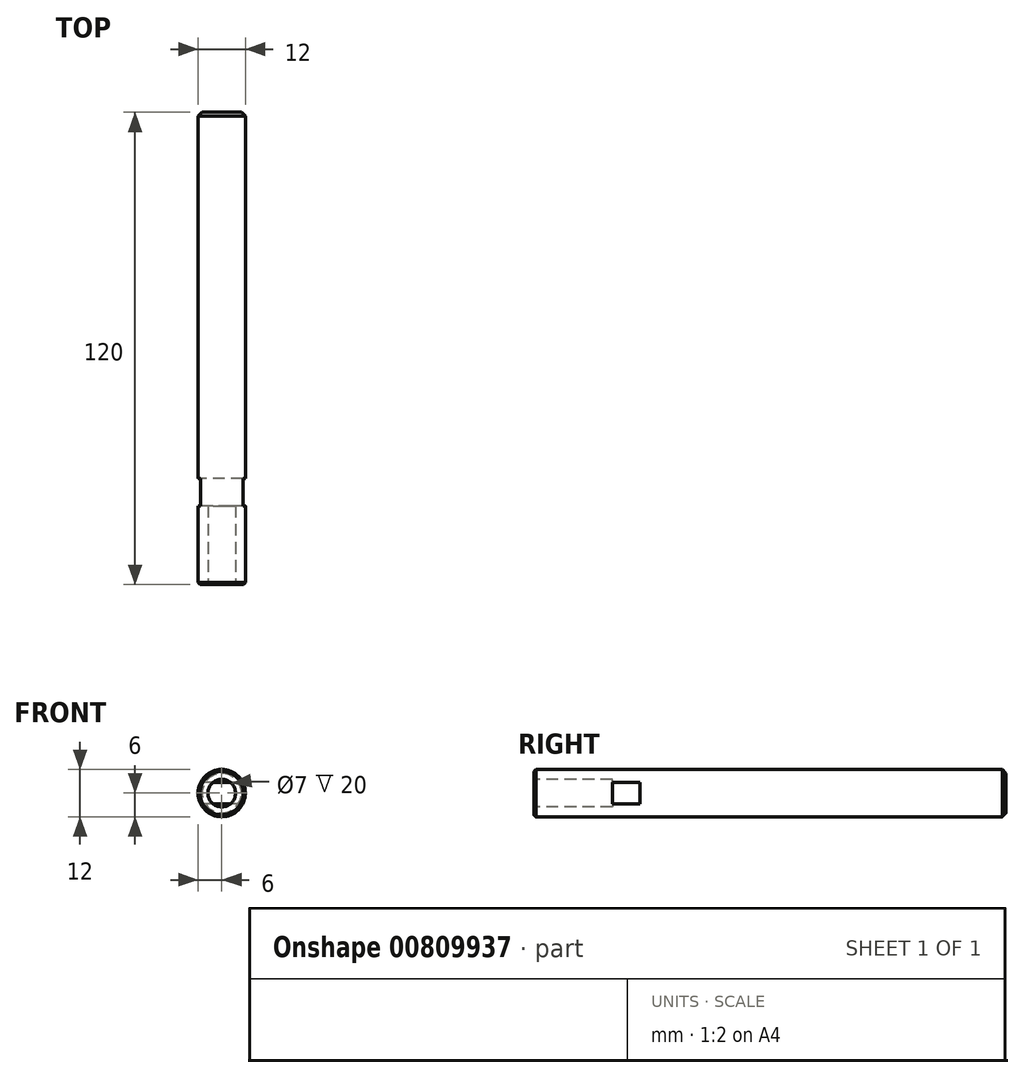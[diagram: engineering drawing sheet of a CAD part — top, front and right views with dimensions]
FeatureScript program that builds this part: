
annotation { "Feature Type Name" : "Feature", "Feature Type Description" : "" }
export const myFeature = defineFeature(function(context is Context, id is Id, definition is map)
    precondition{}
    {
        {
            var Q0;
            Q0=qCreatedBy(makeId("Front.planeOp"),FACE);
            var sketch = newSketch(context, id + "F0", { "sketchPlane" : qUnion([Q0])});
            skCircle(sketch, "E0", {"center": v(0, 0) * mm, "radius": 6 * mm});
            skSolve(sketch);
        }
        {
            var Q0;
            Q0 = qSketchRegion(id + "F0", true);
            extrude(context, id + "F1", {"entities" : qUnion([Q0]), "depth" : 120 * mm, "offsetDistance" : 25 * mm});
        }
        {
            var Q0;
            Q0=makeQuery(id+"F1.opExtrude","CAP_FACE",FACE,{"disambiguationData":[OSD([sQuery(id+"F0.wireOp",EDGE,"E0")])],"isStart":false});
            var sketch = newSketch(context, id + "F2", { "sketchPlane" : qUnion([Q0])});
            skCircle(sketch, "E1", {"center": v(0, 0) * mm, "radius": 3.5 * mm});
            skSolve(sketch);
        }
        {
            var Q0;
            Q0 = qSketchRegion(id + "F2", true);
            extrude(context, id + "F3", {"entities" : qUnion([Q0]), "operationType" : NewBodyOperationType.REMOVE, "oppositeDirection" : true, "depth" : 20 * mm, "offsetDistance" : 25 * mm});
        }
        {
            var Q0;
            Q0=qCreatedBy(makeId("Right.planeOp"),FACE);
            var sketch = newSketch(context, id + "F4", { "sketchPlane" : qUnion([Q0])});
            skLineSegment(sketch, "E2.bottom", {"start": v(-1.8, -7.03) * mm, "end": v(1.8, -7.03) * mm});
            skLineSegment(sketch, "E2.top", {"start": v(-1.8, 7.03) * mm, "end": v(1.8, 7.03) * mm});
            skLineSegment(sketch, "E2.left", {"start": v(-1.8, -7.03) * mm, "end": v(-1.8, 7.03) * mm});
            skLineSegment(sketch, "E2.right", {"start": v(1.8, -7.03) * mm, "end": v(1.8, 7.03) * mm});
            skPoint(sketch, "E2.middle", {"position": v(0, 0) * mm});
            skSolve(sketch);
        }
        {
            var Q0;
            Q0=makeQuery(id+"F1.opExtrude","CAP_EDGE",EDGE,{"disambiguationData":[OSD([sQuery(id+"F0.wireOp",EDGE,"E0")])],"isStart":true});
            chamfer(context, id + "F5", {"entities" : qUnion([Q0]), "width" : 1 * mm, "tangentPropagation" : true});
        }
        {
            var Q0;
            Q0=makeQuery(id+"F1.opExtrude","CAP_EDGE",EDGE,{"disambiguationData":[OSD([sQuery(id+"F0.wireOp",EDGE,"E0")])],"isStart":false});
            chamfer(context, id + "F6", {"entities" : qUnion([Q0]), "width" : .5 * mm, "tangentPropagation" : true});
        }
        {
            var Q0;
            Q0=qCreatedBy(makeId("Right.planeOp"),FACE);
            var sketch = newSketch(context, id + "F7", { "sketchPlane" : qUnion([Q0])});
            skPoint(sketch, "E3", {"position": v(-100, 0) * mm});
            skLineSegment(sketch, "E4", {"start": v(-100, 0) * mm, "end": v(-93, 0) * mm});
            skLineSegment(sketch, "E5.bottom", {"start": v(-100, -2.68) * mm, "end": v(-93, -2.68) * mm});
            skLineSegment(sketch, "E5.top", {"start": v(-100, 2.68) * mm, "end": v(-93, 2.68) * mm});
            skLineSegment(sketch, "E5.left", {"start": v(-100, -2.68) * mm, "end": v(-100, 2.68) * mm});
            skLineSegment(sketch, "E5.right", {"start": v(-93, -2.68) * mm, "end": v(-93, 2.68) * mm});
            skPoint(sketch, "E5.middle", {"position": v(-96.5, 0) * mm});
            skSolve(sketch);
        }
        {
            var Q0;
            Q0 = qSketchRegion(id + "F7", true);
            extrude(context, id + "F8", {"entities" : qUnion([Q0]), "operationType" : NewBodyOperationType.REMOVE, "endBound" : BoundingType.SYMMETRIC, "depth" : 25 * mm, "offsetDistance" : 25 * mm});
        }
    });
